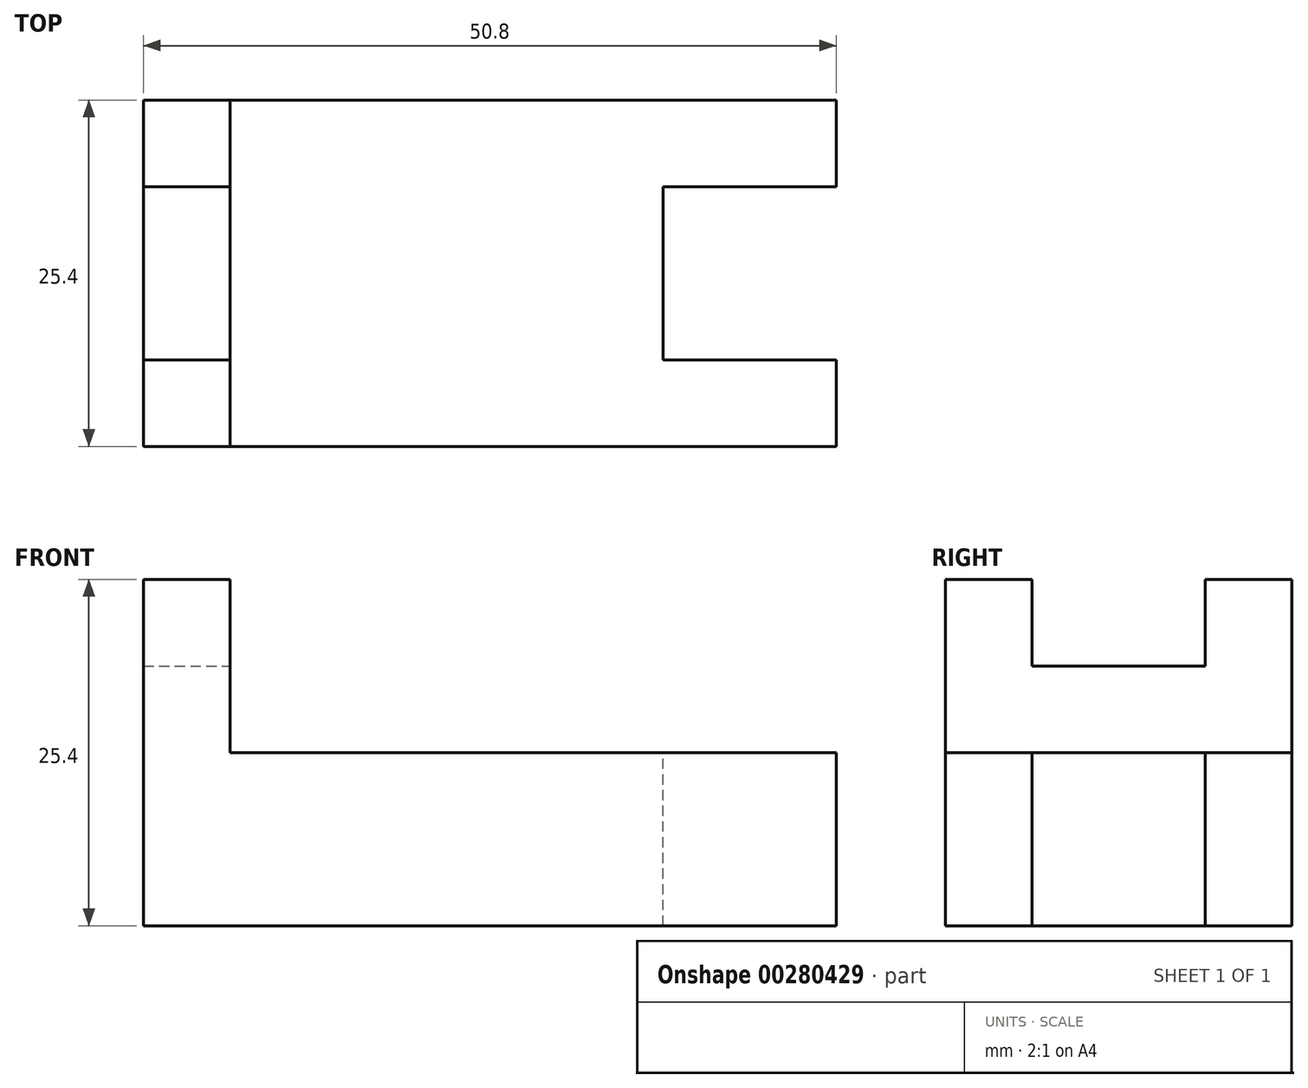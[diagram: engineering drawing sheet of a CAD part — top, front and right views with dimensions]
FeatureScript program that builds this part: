
annotation { "Feature Type Name" : "Feature", "Feature Type Description" : "" }
export const myFeature = defineFeature(function(context is Context, id is Id, definition is map)
    precondition{}
    {
        {
            var Q0;
            Q0=qCreatedBy(makeId("Front.planeOp"),FACE);
            var sketch = newSketch(context, id + "F0", { "sketchPlane" : qUnion([Q0])});
            skLineSegment(sketch, "E0", {"start": v(0, 0) * mm, "end": v(50.8, 0) * mm});
            skLineSegment(sketch, "E1", {"start": v(50.8, 0) * mm, "end": v(50.8, 12.7) * mm});
            skLineSegment(sketch, "E2", {"start": v(50.8, 12.7) * mm, "end": v(6.35, 12.7) * mm});
            skLineSegment(sketch, "E3", {"start": v(6.35, 12.7) * mm, "end": v(6.35, 25.4) * mm});
            skLineSegment(sketch, "E4", {"start": v(6.35, 25.4) * mm, "end": v(0, 25.4) * mm});
            skLineSegment(sketch, "E5", {"start": v(0, 25.4) * mm, "end": v(0, 0) * mm});
            skSolve(sketch);
        }
        {
            var Q0;
            Q0=qSketchRegion(id+"F0",true);
            extrude(context, id + "F1", {"entities" : qUnion([Q0]), "endBound" : BoundingType.SYMMETRIC, "depth" : 25.4 * mm});
        }
        {
            var Q0;
            Q0=makeQuery(id+"F1.opExtrude","SWEPT_FACE",FACE,{"disambiguationData":[OSD([sQuery(id+"F0.wireOp",EDGE,"E4")])]});
            var sketch = newSketch(context, id + "F2", { "sketchPlane" : qUnion([Q0])});
            skLineSegment(sketch, "E6", {"start": v(0, -6.35) * mm, "end": v(6.35, -6.35) * mm});
            skLineSegment(sketch, "E7", {"start": v(6.35, -6.35) * mm, "end": v(6.35, 6.35) * mm});
            skLineSegment(sketch, "E8", {"start": v(6.35, 6.35) * mm, "end": v(0, 6.35) * mm});
            skLineSegment(sketch, "E9", {"start": v(0, 6.35) * mm, "end": v(0, -6.35) * mm});
            skLineSegment(sketch, "E10", {"start": v(0, 6.35) * mm, "end": v(0, 12.7) * mm});
            skLineSegment(sketch, "E11", {"start": v(0, -12.7) * mm, "end": v(0, -6.35) * mm});
            skSolve(sketch);
        }
        {
            var Q0;
            Q0=makeQuery(id+"F2.imprint","IMPRINT",FACE,{"disambiguationData":[TD([[makeQuery(id+"F2.imprint","IMPRINT",EDGE,{"derivedFrom":sQuery(id+"F2.wireOp",EDGE,"E6")}),1.0]])]});
            extrude(context, id + "F3", {"entities" : qUnion([Q0]), "operationType" : NewBodyOperationType.REMOVE, "oppositeDirection" : true, "depth" : 6.35 * mm});
        }
        {
            var Q0;
            Q0=makeQuery(id+"F1.opExtrude","SWEPT_FACE",FACE,{"disambiguationData":[OSD([sQuery(id+"F0.wireOp",EDGE,"E2")])]});
            var sketch = newSketch(context, id + "F4", { "sketchPlane" : qUnion([Q0])});
            skLineSegment(sketch, "E12", {"start": v(50.8, 6.35) * mm, "end": v(38.1, 6.35) * mm});
            skLineSegment(sketch, "E13", {"start": v(38.1, 6.35) * mm, "end": v(38.1, -6.35) * mm});
            skLineSegment(sketch, "E14", {"start": v(38.1, -6.35) * mm, "end": v(50.8, -6.35) * mm});
            skLineSegment(sketch, "E15", {"start": v(50.8, 6.35) * mm, "end": v(50.8, -6.35) * mm});
            skSolve(sketch);
        }
        {
            var Q0;
            Q0=makeQuery(id+"F4.imprint","IMPRINT",FACE,{"disambiguationData":[TD([[makeQuery(id+"F4.imprint","IMPRINT",EDGE,{"derivedFrom":sQuery(id+"F4.wireOp",EDGE,"E12")}),1.0]])]});
            extrude(context, id + "F5", {"entities" : qUnion([Q0]), "operationType" : NewBodyOperationType.REMOVE, "endBound" : BoundingType.THROUGH_ALL, "oppositeDirection" : true, "depth" : 25.4 * mm});
        }
    });
